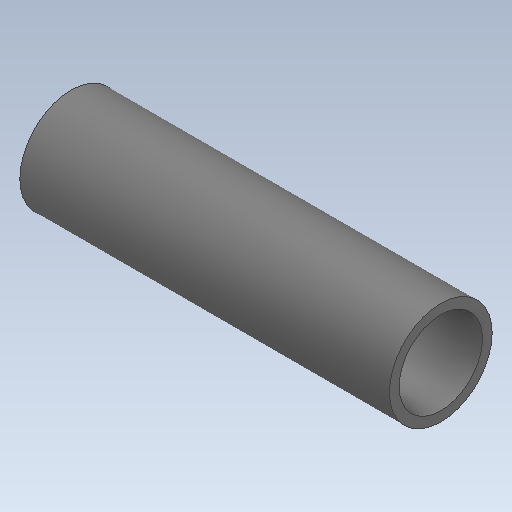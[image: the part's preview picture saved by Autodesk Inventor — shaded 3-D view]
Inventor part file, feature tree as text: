
AUTODESK INVENTOR PART (.ipt)
format: ipt  version: 2020 (Build 240168000, 168)  size: 104,960 bytes
history: native  units: in
note: dims shown in document units (in); Inventor stores cm internally (conversion verified against a paired STEP export)
features: extrude x1
ambient origin geometry x8: Origin, YZ Plane, XZ Plane, XY Plane, X Axis, Y Axis, Z Axis, Center Point
bodies: Solid1 (feature_tree)
feature tree (1):
  extrude  "Extrude-Thin1"  [1 undecoded]
note: 1 required parameter value undecoded (feature->parameter linkage not recoverable at this tier; creation-order binding heuristic only, values carry confidence <= 0.55)
